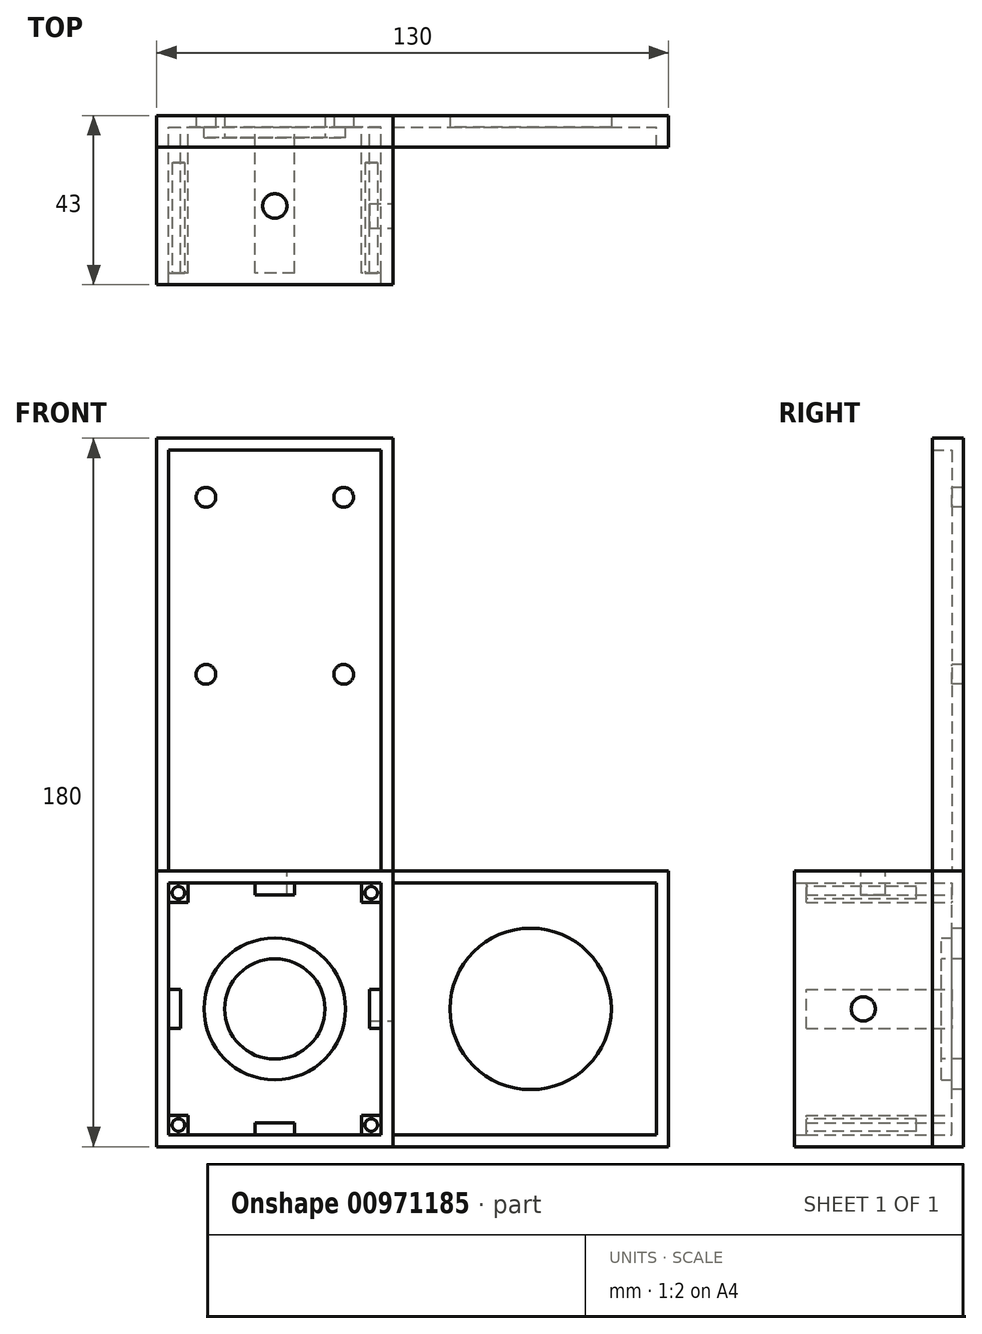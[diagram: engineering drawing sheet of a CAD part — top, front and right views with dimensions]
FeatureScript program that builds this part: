
annotation { "Feature Type Name" : "Feature", "Feature Type Description" : "" }
export const myFeature = defineFeature(function(context is Context, id is Id, definition is map)
    precondition{}
    {
        {
            var Q0;
            Q0=qCreatedBy(makeId("Front.planeOp"),FACE);
            var sketch = newSketch(context, id + "F0", { "sketchPlane" : qUnion([Q0])});
            skLineSegment(sketch, "E0.bottom", {"start": v(30, -90) * mm, "end": v(-30, -90) * mm});
            skLineSegment(sketch, "E0.top", {"start": v(30, 90) * mm, "end": v(-30, 90) * mm});
            skLineSegment(sketch, "E0.left", {"start": v(30, -90) * mm, "end": v(30, 90) * mm});
            skLineSegment(sketch, "E0.right", {"start": v(-30, -90) * mm, "end": v(-30, 90) * mm});
            skPoint(sketch, "E0.middle", {"position": v(0, 0) * mm});
            skCircle(sketch, "E1", {"center": v(0, -55) * mm, "radius": 12.75 * mm});
            skCircle(sketch, "E2", {"center": v(-17.5, 75) * mm, "radius": 2.5 * mm});
            skCircle(sketch, "E3", {"center": v(17.5, 75) * mm, "radius": 2.5 * mm});
            skCircle(sketch, "E4", {"center": v(-17.5, 30) * mm, "radius": 2.5 * mm});
            skCircle(sketch, "E5", {"center": v(17.5, 30) * mm, "radius": 2.5 * mm});
            skSolve(sketch);
        }
        {
            var Q0;
            Q0=makeQuery(id+"F0.imprint","IMPRINT",FACE,{"disambiguationData":[TD([[makeQuery(id+"F0.imprint","IMPRINT",EDGE,{"derivedFrom":sQuery(id+"F0.wireOp",EDGE,"E0.bottom")}),-1.0]])]});
            extrude(context, id + "F1", {"entities" : qUnion([Q0]), "oppositeDirection" : true, "depth" : 3 * mm, "offsetDistance" : 25 * mm});
        }
        {
            var Q0;
            Q0=makeQuery(id+"F1.opExtrude","CAP_FACE",FACE,{"disambiguationData":[OSD([sQuery(id+"F0.wireOp",EDGE,"E0.bottom"),sQuery(id+"F0.wireOp",EDGE,"E0.top"),sQuery(id+"F0.wireOp",EDGE,"E0.left"),sQuery(id+"F0.wireOp",EDGE,"E0.right"),sQuery(id+"F0.wireOp",EDGE,"E1")])],"isStart":true});
            var sketch = newSketch(context, id + "F2", { "sketchPlane" : qUnion([Q0])});
            skCircle(sketch, "E6", {"center": v(0, -55) * mm, "radius": 18 * mm});
            skSolve(sketch);
        }
        {
            var Q0;
            Q0=makeQuery(id+"F2.imprint","IMPRINT",FACE,{"disambiguationData":[TD([[makeQuery(id+"F2.imprint","IMPRINT",EDGE,{"derivedFrom":sQuery(id+"F2.wireOp",EDGE,"E6")}),1.0]])]});
            extrude(context, id + "F3", {"entities" : qUnion([Q0]), "operationType" : NewBodyOperationType.ADD, "depth" : 2.6 * mm, "offsetDistance" : 25 * mm});
        }
        {
            var Q0;
            Q0=makeQuery(id+"F1.opExtrude","CAP_FACE",FACE,{"disambiguationData":[OSD([sQuery(id+"F0.wireOp",EDGE,"E0.bottom"),sQuery(id+"F0.wireOp",EDGE,"E0.top"),sQuery(id+"F0.wireOp",EDGE,"E0.left"),sQuery(id+"F0.wireOp",EDGE,"E0.right"),sQuery(id+"F0.wireOp",EDGE,"E1")])],"isStart":true});
            var sketch = newSketch(context, id + "F4", { "sketchPlane" : qUnion([Q0])});
            skLineSegment(sketch, "E7.bottom", {"start": v(-30, -90) * mm, "end": v(30, -90) * mm});
            skLineSegment(sketch, "E7.top", {"start": v(-30, -20) * mm, "end": v(30, -20) * mm});
            skLineSegment(sketch, "E7.left", {"start": v(-30, -90) * mm, "end": v(-30, -20) * mm});
            skLineSegment(sketch, "E7.right", {"start": v(30, -90) * mm, "end": v(30, -20) * mm});
            skPoint(sketch, "E8", {"position": v(30, 0) * mm});
            skLineSegment(sketch, "E9", {"start": v(-27, -23) * mm, "end": v(27, -23) * mm});
            skLineSegment(sketch, "E10", {"start": v(27, -23) * mm, "end": v(27, -87) * mm});
            skLineSegment(sketch, "E11", {"start": v(27, -87) * mm, "end": v(-27, -87) * mm});
            skLineSegment(sketch, "E12", {"start": v(-27, -87) * mm, "end": v(-27, -23) * mm});
            skSolve(sketch);
        }
        {
            var Q0;
            Q0=makeQuery(id+"F4.imprint","IMPRINT",FACE,{"disambiguationData":[TD([[makeQuery(id+"F4.imprint","IMPRINT",EDGE,{"derivedFrom":sQuery(id+"F4.wireOp",EDGE,"E7.bottom")}),-1.0]])]});
            extrude(context, id + "F5", {"entities" : qUnion([Q0]), "operationType" : NewBodyOperationType.ADD, "depth" : 40 * mm, "offsetDistance" : 25 * mm});
        }
        {
            var Q0;
            Q0=makeQuery(id+"F5.boolean.opBoolean","SPLIT",FACE,{"disambiguationData":[TD([makeQuery(id+"F3.opExtrude","SWEPT_FACE",FACE,{"disambiguationData":[OSD([sQuery(id+"F2.wireOp",EDGE,"E6")])]})])],"derivedFrom":makeQuery(id+"F1.opExtrude","CAP_FACE",FACE,{"disambiguationData":[OSD([sQuery(id+"F0.wireOp",EDGE,"E0.bottom"),sQuery(id+"F0.wireOp",EDGE,"E0.top"),sQuery(id+"F0.wireOp",EDGE,"E0.left"),sQuery(id+"F0.wireOp",EDGE,"E0.right"),sQuery(id+"F0.wireOp",EDGE,"E1")])],"isStart":true})});
            var sketch = newSketch(context, id + "F6", { "sketchPlane" : qUnion([Q0])});
            skLineSegment(sketch, "E13.bottom", {"start": v(27, -23) * mm, "end": v(22, -23) * mm});
            skLineSegment(sketch, "E13.top", {"start": v(27, -28) * mm, "end": v(22, -28) * mm});
            skLineSegment(sketch, "E13.left", {"start": v(27, -23) * mm, "end": v(27, -28) * mm});
            skLineSegment(sketch, "E13.right", {"start": v(22, -23) * mm, "end": v(22, -28) * mm});
            skLineSegment(sketch, "E14.bottom", {"start": v(-27, -23) * mm, "end": v(-22, -23) * mm});
            skLineSegment(sketch, "E14.top", {"start": v(-27, -28) * mm, "end": v(-22, -28) * mm});
            skLineSegment(sketch, "E14.left", {"start": v(-27, -23) * mm, "end": v(-27, -28) * mm});
            skLineSegment(sketch, "E14.right", {"start": v(-22, -23) * mm, "end": v(-22, -28) * mm});
            skLineSegment(sketch, "E15.bottom", {"start": v(-27, -87) * mm, "end": v(-22, -87) * mm});
            skLineSegment(sketch, "E15.top", {"start": v(-27, -82) * mm, "end": v(-22, -82) * mm});
            skLineSegment(sketch, "E15.left", {"start": v(-27, -87) * mm, "end": v(-27, -82) * mm});
            skLineSegment(sketch, "E15.right", {"start": v(-22, -87) * mm, "end": v(-22, -82) * mm});
            skLineSegment(sketch, "E16.bottom", {"start": v(27, -87) * mm, "end": v(22, -87) * mm});
            skLineSegment(sketch, "E16.top", {"start": v(27, -82) * mm, "end": v(22, -82) * mm});
            skLineSegment(sketch, "E16.left", {"start": v(27, -87) * mm, "end": v(27, -82) * mm});
            skLineSegment(sketch, "E16.right", {"start": v(22, -87) * mm, "end": v(22, -82) * mm});
            skLineSegment(sketch, "E17.bottom", {"start": v(-5, -23) * mm, "end": v(5, -23) * mm});
            skLineSegment(sketch, "E17.top", {"start": v(-5, -26) * mm, "end": v(5, -26) * mm});
            skLineSegment(sketch, "E17.left", {"start": v(-5, -23) * mm, "end": v(-5, -26) * mm});
            skLineSegment(sketch, "E17.right", {"start": v(5, -23) * mm, "end": v(5, -26) * mm});
            skLineSegment(sketch, "E18.bottom", {"start": v(-5, -87) * mm, "end": v(5, -87) * mm});
            skLineSegment(sketch, "E18.top", {"start": v(-5, -84) * mm, "end": v(5, -84) * mm});
            skLineSegment(sketch, "E18.left", {"start": v(-5, -87) * mm, "end": v(-5, -84) * mm});
            skLineSegment(sketch, "E18.right", {"start": v(5, -87) * mm, "end": v(5, -84) * mm});
            skLineSegment(sketch, "E19.bottom", {"start": v(27, -50) * mm, "end": v(24, -50) * mm});
            skLineSegment(sketch, "E19.top", {"start": v(27, -60) * mm, "end": v(24, -60) * mm});
            skLineSegment(sketch, "E19.left", {"start": v(27, -50) * mm, "end": v(27, -60) * mm});
            skLineSegment(sketch, "E19.right", {"start": v(24, -50) * mm, "end": v(24, -60) * mm});
            skLineSegment(sketch, "E20.bottom", {"start": v(-27, -50) * mm, "end": v(-24, -50) * mm});
            skLineSegment(sketch, "E20.top", {"start": v(-27, -60) * mm, "end": v(-24, -60) * mm});
            skLineSegment(sketch, "E20.left", {"start": v(-27, -50) * mm, "end": v(-27, -60) * mm});
            skLineSegment(sketch, "E20.right", {"start": v(-24, -50) * mm, "end": v(-24, -60) * mm});
            skLineSegment(sketch, "E21", {"start": v(0, -33.43) * mm, "end": v(0, -77.94) * mm, "construction": true});
            skSolve(sketch);
        }
        {
            var Q0;
            Q0=makeQuery(id+"F6.imprint","IMPRINT",FACE,{"disambiguationData":[TD([[makeQuery(id+"F6.imprint","IMPRINT",EDGE,{"derivedFrom":sQuery(id+"F6.wireOp",EDGE,"E14.bottom")}),-1.0]])]});
            var Q1;
            Q1=makeQuery(id+"F6.imprint","IMPRINT",FACE,{"disambiguationData":[TD([[makeQuery(id+"F6.imprint","IMPRINT",EDGE,{"derivedFrom":sQuery(id+"F6.wireOp",EDGE,"E17.bottom")}),-1.0]])]});
            var Q2;
            Q2=makeQuery(id+"F6.imprint","IMPRINT",FACE,{"disambiguationData":[TD([[makeQuery(id+"F6.imprint","IMPRINT",EDGE,{"derivedFrom":sQuery(id+"F6.wireOp",EDGE,"E13.bottom")}),-1.0]])]});
            var Q3;
            Q3=makeQuery(id+"F6.imprint","IMPRINT",FACE,{"disambiguationData":[TD([[makeQuery(id+"F6.imprint","IMPRINT",EDGE,{"derivedFrom":sQuery(id+"F6.wireOp",EDGE,"E19.bottom")}),1.0]])]});
            var Q4;
            Q4=makeQuery(id+"F6.imprint","IMPRINT",FACE,{"disambiguationData":[TD([[makeQuery(id+"F6.imprint","IMPRINT",EDGE,{"derivedFrom":sQuery(id+"F6.wireOp",EDGE,"E20.bottom")}),-1.0]])]});
            var Q5;
            Q5=makeQuery(id+"F6.imprint","IMPRINT",FACE,{"disambiguationData":[TD([[makeQuery(id+"F6.imprint","IMPRINT",EDGE,{"derivedFrom":sQuery(id+"F6.wireOp",EDGE,"E16.bottom")}),-1.0]])]});
            var Q6;
            Q6=makeQuery(id+"F6.imprint","IMPRINT",FACE,{"disambiguationData":[TD([[makeQuery(id+"F6.imprint","IMPRINT",EDGE,{"derivedFrom":sQuery(id+"F6.wireOp",EDGE,"E18.bottom")}),-1.0]])]});
            var Q7;
            Q7=makeQuery(id+"F6.imprint","IMPRINT",FACE,{"disambiguationData":[TD([[makeQuery(id+"F6.imprint","IMPRINT",EDGE,{"derivedFrom":sQuery(id+"F6.wireOp",EDGE,"E15.bottom")}),-1.0]])]});
            extrude(context, id + "F7", {"entities" : qUnion([Q0, Q1, Q2, Q3, Q4, Q5, Q6, Q7]), "operationType" : NewBodyOperationType.ADD, "depth" : 37 * mm, "offsetDistance" : 25 * mm});
        }
        {
            var Q0;
            Q0=makeQuery(id+"F7.opExtrude","CAP_FACE",FACE,{"disambiguationData":[OSD([sQuery(id+"F6.wireOp",EDGE,"E13.bottom"),sQuery(id+"F6.wireOp",EDGE,"E13.top"),sQuery(id+"F6.wireOp",EDGE,"E13.left"),sQuery(id+"F6.wireOp",EDGE,"E13.right")])],"isStart":false});
            var sketch = newSketch(context, id + "F8", { "sketchPlane" : qUnion([Q0])});
            skCircle(sketch, "E22", {"center": v(24.5, -25.5) * mm, "radius": 1.6 * mm});
            skCircle(sketch, "E23", {"center": v(-24.5, -25.5) * mm, "radius": 1.6 * mm});
            skCircle(sketch, "E24", {"center": v(-24.5, -84.5) * mm, "radius": 1.6 * mm});
            skCircle(sketch, "E25", {"center": v(24.5, -84.5) * mm, "radius": 1.6 * mm});
            skSolve(sketch);
        }
        {
            var Q0;
            Q0=makeQuery(id+"F8.imprint","IMPRINT",FACE,{"disambiguationData":[TD([[makeQuery(id+"F8.imprint","IMPRINT",EDGE,{"derivedFrom":sQuery(id+"F8.wireOp",EDGE,"E22")}),1.0]])]});
            var Q1;
            Q1=makeQuery(id+"F8.imprint","IMPRINT",FACE,{"disambiguationData":[TD([[makeQuery(id+"F8.imprint","IMPRINT",EDGE,{"derivedFrom":sQuery(id+"F8.wireOp",EDGE,"E23")}),1.0]])]});
            var Q2;
            Q2=makeQuery(id+"F8.imprint","IMPRINT",FACE,{"disambiguationData":[TD([[makeQuery(id+"F8.imprint","IMPRINT",EDGE,{"derivedFrom":sQuery(id+"F8.wireOp",EDGE,"E25")}),1.0]])]});
            var Q3;
            Q3=makeQuery(id+"F8.imprint","IMPRINT",FACE,{"disambiguationData":[TD([[makeQuery(id+"F8.imprint","IMPRINT",EDGE,{"derivedFrom":sQuery(id+"F8.wireOp",EDGE,"E24")}),1.0]])]});
            extrude(context, id + "F9", {"entities" : qUnion([Q0, Q1, Q2, Q3]), "operationType" : NewBodyOperationType.REMOVE, "oppositeDirection" : true, "depth" : 28 * mm, "offsetDistance" : 25 * mm});
        }
        {
            var Q0;
            Q0=makeQuery(id+"F5.boolean.opBoolean","MERGE",FACE,{"derivedFrom":[makeQuery(id+"F1.opExtrude","SWEPT_FACE",FACE,{"disambiguationData":[OSD([sQuery(id+"F0.wireOp",EDGE,"E0.left")])]}),makeQuery(id+"F5.opExtrude","SWEPT_FACE",FACE,{"disambiguationData":[OSD([sQuery(id+"F4.wireOp",EDGE,"E7.right")])]})]});
            var sketch = newSketch(context, id + "F10", { "sketchPlane" : qUnion([Q0])});
            skLineSegment(sketch, "E26.bottom", {"start": v(3, -90) * mm, "end": v(0, -90) * mm});
            skLineSegment(sketch, "E26.top", {"start": v(3, -20) * mm, "end": v(0, -20) * mm});
            skLineSegment(sketch, "E26.left", {"start": v(3, -90) * mm, "end": v(3, -20) * mm});
            skLineSegment(sketch, "E26.right", {"start": v(0, -90) * mm, "end": v(0, -20) * mm});
            skSolve(sketch);
        }
        {
            var Q0;
            Q0=makeQuery(id+"F10.imprint","IMPRINT",FACE,{"disambiguationData":[TD([[makeQuery(id+"F10.imprint","IMPRINT",EDGE,{"derivedFrom":sQuery(id+"F10.wireOp",EDGE,"E26.bottom")}),-1.0]])]});
            extrude(context, id + "F11", {"entities" : qUnion([Q0]), "operationType" : NewBodyOperationType.ADD, "depth" : 70 * mm, "offsetDistance" : 25 * mm});
        }
        {
            var Q0;
            Q0=makeQuery(id+"F11.opExtrude","SWEPT_FACE",FACE,{"disambiguationData":[OSD([sQuery(id+"F10.wireOp",EDGE,"E26.right")])]});
            var sketch = newSketch(context, id + "F12", { "sketchPlane" : qUnion([Q0])});
            skLineSegment(sketch, "E27", {"start": v(30, -55) * mm, "end": v(128.66, -55) * mm, "construction": true});
            skPoint(sketch, "E27.endSnap0", {"position": v(100, -55) * mm});
            skLineSegment(sketch, "E28", {"start": v(65, 0) * mm, "end": v(65, -99.6) * mm, "construction": true});
            skPoint(sketch, "E28.startSnap0", {"position": v(65, -20) * mm});
            skSolve(sketch);
        }
        {
            var Q0;
            {var subQ0=sQuery(id+"F10.wireOp",EDGE,"E26.right");Q0=makeQuery(id+"F12.imprint","IMPRINT",FACE,{"disambiguationData":[TD([[makeQuery(id+"F12.imprint","IMPRINT",EDGE,{"derivedFrom":makeQuery(id+"F11.opExtrude","CAP_EDGE",EDGE,{"disambiguationData":[OSD([subQ0])],"isStart":false})}),1.0]])]});}
            var sketch = newSketch(context, id + "F13", { "sketchPlane" : qUnion([Q0])});
            skCircle(sketch, "E29", {"center": v(65, -55) * mm, "radius": 20.5 * mm});
            skSolve(sketch);
        }
        {
            var Q0;
            Q0=makeQuery(id+"F13.imprint","IMPRINT",FACE,{"disambiguationData":[TD([[makeQuery(id+"F13.imprint","IMPRINT",EDGE,{"derivedFrom":sQuery(id+"F13.wireOp",EDGE,"E29")}),1.0]])]});
            extrude(context, id + "F14", {"entities" : qUnion([Q0]), "operationType" : NewBodyOperationType.REMOVE, "endBound" : BoundingType.UP_TO_NEXT, "oppositeDirection" : true, "depth" : 25 * mm, "offsetDistance" : 25 * mm});
        }
        {
            var Q0;
            {var subQ0=sQuery(id+"F10.wireOp",EDGE,"E26.right");Q0=makeQuery(id+"F12.imprint","IMPRINT",FACE,{"disambiguationData":[TD([[makeQuery(id+"F12.imprint","IMPRINT",EDGE,{"derivedFrom":makeQuery(id+"F11.opExtrude","CAP_EDGE",EDGE,{"disambiguationData":[OSD([subQ0])],"isStart":false})}),1.0]])]});}
            var sketch = newSketch(context, id + "F15", { "sketchPlane" : qUnion([Q0])});
            skLineSegment(sketch, "E30.bottom", {"start": v(30, -20) * mm, "end": v(100, -20) * mm});
            skLineSegment(sketch, "E30.top", {"start": v(30, -23) * mm, "end": v(97, -23) * mm});
            skLineSegment(sketch, "E30.left", {"start": v(30, -20) * mm, "end": v(30, -23) * mm});
            skLineSegment(sketch, "E30.right", {"start": v(100, -20) * mm, "end": v(100, -23) * mm});
            skLineSegment(sketch, "E31.bottom", {"start": v(30, -87) * mm, "end": v(97, -87) * mm});
            skLineSegment(sketch, "E31.top", {"start": v(30, -90) * mm, "end": v(100, -90) * mm});
            skLineSegment(sketch, "E31.left", {"start": v(30, -87) * mm, "end": v(30, -90) * mm});
            skLineSegment(sketch, "E31.right", {"start": v(100, -87) * mm, "end": v(100, -90) * mm});
            skLineSegment(sketch, "E32.left", {"start": v(100, -23) * mm, "end": v(100, -87) * mm});
            skLineSegment(sketch, "E32.right", {"start": v(97, -23) * mm, "end": v(97, -87) * mm});
            skSolve(sketch);
        }
        {
            var Q0;
            Q0=makeQuery(id+"F15.imprint","IMPRINT",FACE,{"disambiguationData":[TD([[makeQuery(id+"F15.imprint","IMPRINT",EDGE,{"derivedFrom":sQuery(id+"F15.wireOp",EDGE,"E30.bottom")}),1.0]])]});
            extrude(context, id + "F16", {"entities" : qUnion([Q0]), "operationType" : NewBodyOperationType.ADD, "depth" : 5 * mm, "offsetDistance" : 25 * mm});
        }
        {
            var Q0;
            {var subQ1=sQuery(id+"F0.wireOp",EDGE,"E0.left");var subQ2=makeQuery(id+"F1.opExtrude","SWEPT_FACE",FACE,{"disambiguationData":[OSD([subQ1])]});var subQ3=sQuery(id+"F0.wireOp",EDGE,"E0.bottom");var subQ4=sQuery(id+"F4.wireOp",EDGE,"E7.right");var subQ5=makeQuery(id+"F5.opExtrude","SWEPT_FACE",FACE,{"disambiguationData":[OSD([subQ4])]});Q0=makeQuery(id+"F11.boolean.opBoolean","SPLIT",FACE,{"disambiguationData":[TD([makeQuery(id+"F1.opExtrude","SWEPT_FACE",FACE,{"disambiguationData":[OSD([subQ3])]})])],"derivedFrom":makeQuery(id+"F5.boolean.opBoolean","MERGE",FACE,{"derivedFrom":[subQ2,subQ5]})});}
            var sketch = newSketch(context, id + "F17", { "sketchPlane" : qUnion([Q0])});
            skCircle(sketch, "E33", {"center": v(-22.5, -55) * mm, "radius": 3.07 * mm});
            skPoint(sketch, "E33.centerSnap0", {"position": v(-22.5, -20) * mm});
            skSolve(sketch);
        }
        {
            var Q0;
            Q0=makeQuery(id+"F17.imprint","IMPRINT",FACE,{"disambiguationData":[TD([[makeQuery(id+"F17.imprint","IMPRINT",EDGE,{"derivedFrom":sQuery(id+"F17.wireOp",EDGE,"E33")}),1.0]])]});
            extrude(context, id + "F18", {"entities" : qUnion([Q0]), "operationType" : NewBodyOperationType.REMOVE, "endBound" : BoundingType.UP_TO_NEXT, "oppositeDirection" : true, "depth" : 25 * mm, "offsetDistance" : 25 * mm});
        }
        {
            var Q0;
            Q0=makeQuery(id+"F16.boolean.opBoolean","MERGE",FACE,{"derivedFrom":[makeQuery(id+"F5.opExtrude","SWEPT_FACE",FACE,{"disambiguationData":[OSD([sQuery(id+"F4.wireOp",EDGE,"E7.top")])]}),makeQuery(id+"F11.opExtrude","SWEPT_FACE",FACE,{"disambiguationData":[OSD([sQuery(id+"F10.wireOp",EDGE,"E26.top")])]}),makeQuery(id+"F16.opExtrude","SWEPT_FACE",FACE,{"disambiguationData":[OSD([sQuery(id+"F15.wireOp",EDGE,"E30.bottom")])]})]});
            var sketch = newSketch(context, id + "F19", { "sketchPlane" : qUnion([Q0])});
            skCircle(sketch, "E34", {"center": v(0, -20) * mm, "radius": 3.1 * mm});
            skPoint(sketch, "E34.centerSnap0", {"position": v(-30, -20) * mm});
            skSolve(sketch);
        }
        {
            var Q0;
            Q0=makeQuery(id+"F19.imprint","IMPRINT",FACE,{"disambiguationData":[TD([[makeQuery(id+"F19.imprint","IMPRINT",EDGE,{"derivedFrom":sQuery(id+"F19.wireOp",EDGE,"E34")}),1.0]])]});
            extrude(context, id + "F20", {"entities" : qUnion([Q0]), "operationType" : NewBodyOperationType.REMOVE, "endBound" : BoundingType.UP_TO_NEXT, "oppositeDirection" : true, "depth" : 25 * mm, "offsetDistance" : 25 * mm});
        }
        {
            var Q0;
            {var subQ0=sQuery(id+"F0.wireOp",EDGE,"E0.right");var subQ1=sQuery(id+"F0.wireOp",EDGE,"E0.left");var subQ2=sQuery(id+"F0.wireOp",EDGE,"E0.top");Q0=makeQuery(id+"F5.boolean.opBoolean","SPLIT",FACE,{"disambiguationData":[TD([makeQuery(id+"F1.opExtrude","SWEPT_FACE",FACE,{"disambiguationData":[OSD([subQ2])]})])],"derivedFrom":makeQuery(id+"F1.opExtrude","CAP_FACE",FACE,{"disambiguationData":[OSD([sQuery(id+"F0.wireOp",EDGE,"E0.bottom"),subQ2,subQ1,subQ0,sQuery(id+"F0.wireOp",EDGE,"E1")])],"isStart":true})});}
            var sketch = newSketch(context, id + "F21", { "sketchPlane" : qUnion([Q0])});
            skLineSegment(sketch, "E35.bottom", {"start": v(30, 90) * mm, "end": v(27, 90) * mm});
            skLineSegment(sketch, "E35.top", {"start": v(30, -20) * mm, "end": v(27, -20) * mm});
            skLineSegment(sketch, "E35.left", {"start": v(30, 90) * mm, "end": v(30, -20) * mm});
            skLineSegment(sketch, "E35.right", {"start": v(27, 87) * mm, "end": v(27, -20) * mm});
            skLineSegment(sketch, "E36.bottom", {"start": v(-30, 90) * mm, "end": v(-27, 90) * mm});
            skLineSegment(sketch, "E36.top", {"start": v(-30, -20) * mm, "end": v(-27, -20) * mm});
            skLineSegment(sketch, "E36.left", {"start": v(-30, 90) * mm, "end": v(-30, -20) * mm});
            skLineSegment(sketch, "E36.right", {"start": v(-27, 87) * mm, "end": v(-27, -20) * mm});
            skLineSegment(sketch, "E37.bottom", {"start": v(-27, 90) * mm, "end": v(21.68, 90) * mm});
            skLineSegment(sketch, "E37.top", {"start": v(-27, 87) * mm, "end": v(27, 87) * mm});
            skSolve(sketch);
        }
        {
            var Q0;
            {var subQ1=sQuery(id+"F21.wireOp",EDGE,"E35.bottom");Q0=makeQuery(id+"F21.imprint","IMPRINT",FACE,{"disambiguationData":[TD([[makeQuery(id+"F21.imprint","IMPRINT",EDGE,{"derivedFrom":subQ1}),1.0]])]});}
            extrude(context, id + "F22", {"entities" : qUnion([Q0]), "operationType" : NewBodyOperationType.ADD, "depth" : 5 * mm, "offsetDistance" : 25 * mm});
        }
    });
